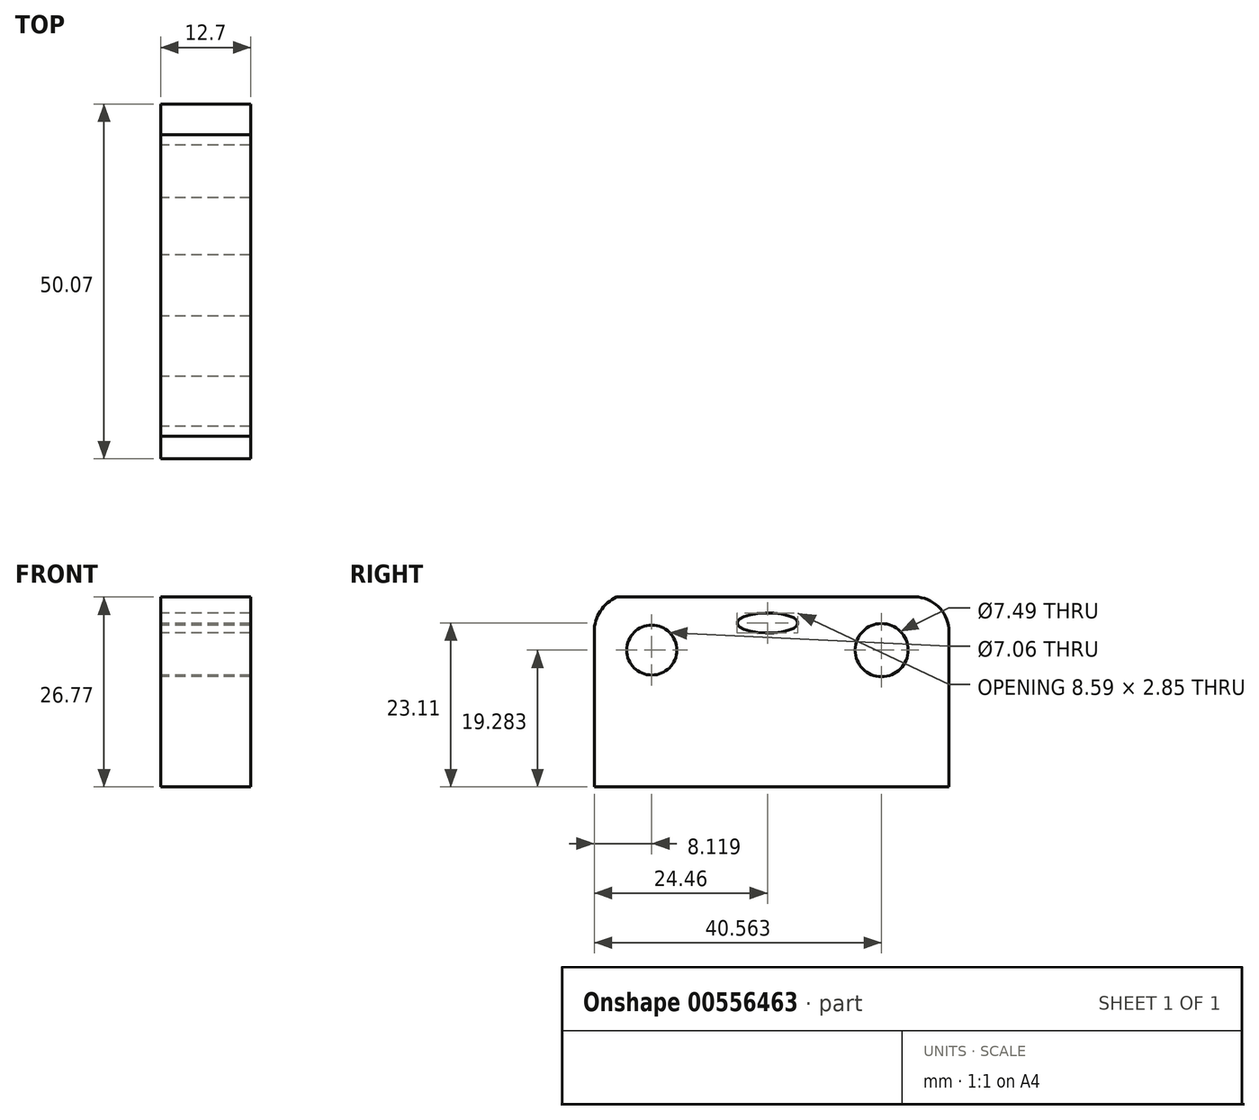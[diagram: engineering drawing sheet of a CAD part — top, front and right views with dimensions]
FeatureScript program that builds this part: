
annotation { "Feature Type Name" : "Feature", "Feature Type Description" : "" }
export const myFeature = defineFeature(function(context is Context, id is Id, definition is map)
    precondition{}
    {
        {
            var Q0;
            Q0=qCreatedBy(makeId("Right.planeOp"),FACE);
            var sketch = newSketch(context, id + "F0", { "sketchPlane" : qUnion([Q0])});
            skLineSegment(sketch, "E0", {"start": v(-24.46, 0) * mm, "end": v(-24.46, 21.87) * mm});
            skLineSegment(sketch, "E1", {"start": v(-21.3, 26.77) * mm, "end": v(0, 26.77) * mm});
            skLineSegment(sketch, "E2", {"start": v(0, 26.77) * mm, "end": v(21.3, 26.77) * mm});
            skLineSegment(sketch, "E3", {"start": v(25.61, 21.87) * mm, "end": v(25.61, 0) * mm});
            skLineSegment(sketch, "E4", {"start": v(25.61, 0) * mm, "end": v(-24.46, 0) * mm});
            skLineSegment(sketch, "E5", {"start": v(-10.65, 26.77) * mm, "end": v(-10.65, 0) * mm});
            skLineSegment(sketch, "E6", {"start": v(10.65, 26.77) * mm, "end": v(10.65, 0) * mm});
            skLineSegment(sketch, "E7", {"start": v(-10.65, 19.28) * mm, "end": v(10.65, 19.28) * mm});
            skCircle(sketch, "E8", {"center": v(-16.34, 19.28) * mm, "radius": 3.53 * mm});
            skCircle(sketch, "E9", {"center": v(16.1, 19.28) * mm, "radius": 3.74 * mm});
            skEllipse(sketch, "E10", {"center": v(0, 23.11) * mm, "majorRadius": 4.3 * mm, "minorRadius": 1.43 * mm, "majorAxis": v(1, 0)});
            skLineSegment(sketch, "E11", {"start": v(-24.46, 0) * mm, "end": v(-15.65, 0) * mm});
            skLineSegment(sketch, "E12", {"start": v(-19.68, 0) * mm, "end": v(-15.65, 0) * mm});
            skArc(sketch, "E13", {"start": v(-21.3, 26.77) * mm, "mid": v(-23.6, 24.79) * mm, "end": v(-24.46, 21.87) * mm});
            skArc(sketch, "E14", {"start": v(25.61, 21.87) * mm, "mid": v(24.38, 25.14) * mm, "end": v(21.3, 26.77) * mm});
            skSolve(sketch);
        }
        {
            var Q0;
            Q0 = qSketchRegion(id + "F0", true);
            extrude(context, id + "F1", {"entities" : qUnion([Q0]), "endBound" : BoundingType.SYMMETRIC, "depth" : 12.7 * mm, "offsetDistance" : 25.4 * mm});
        }
    });
